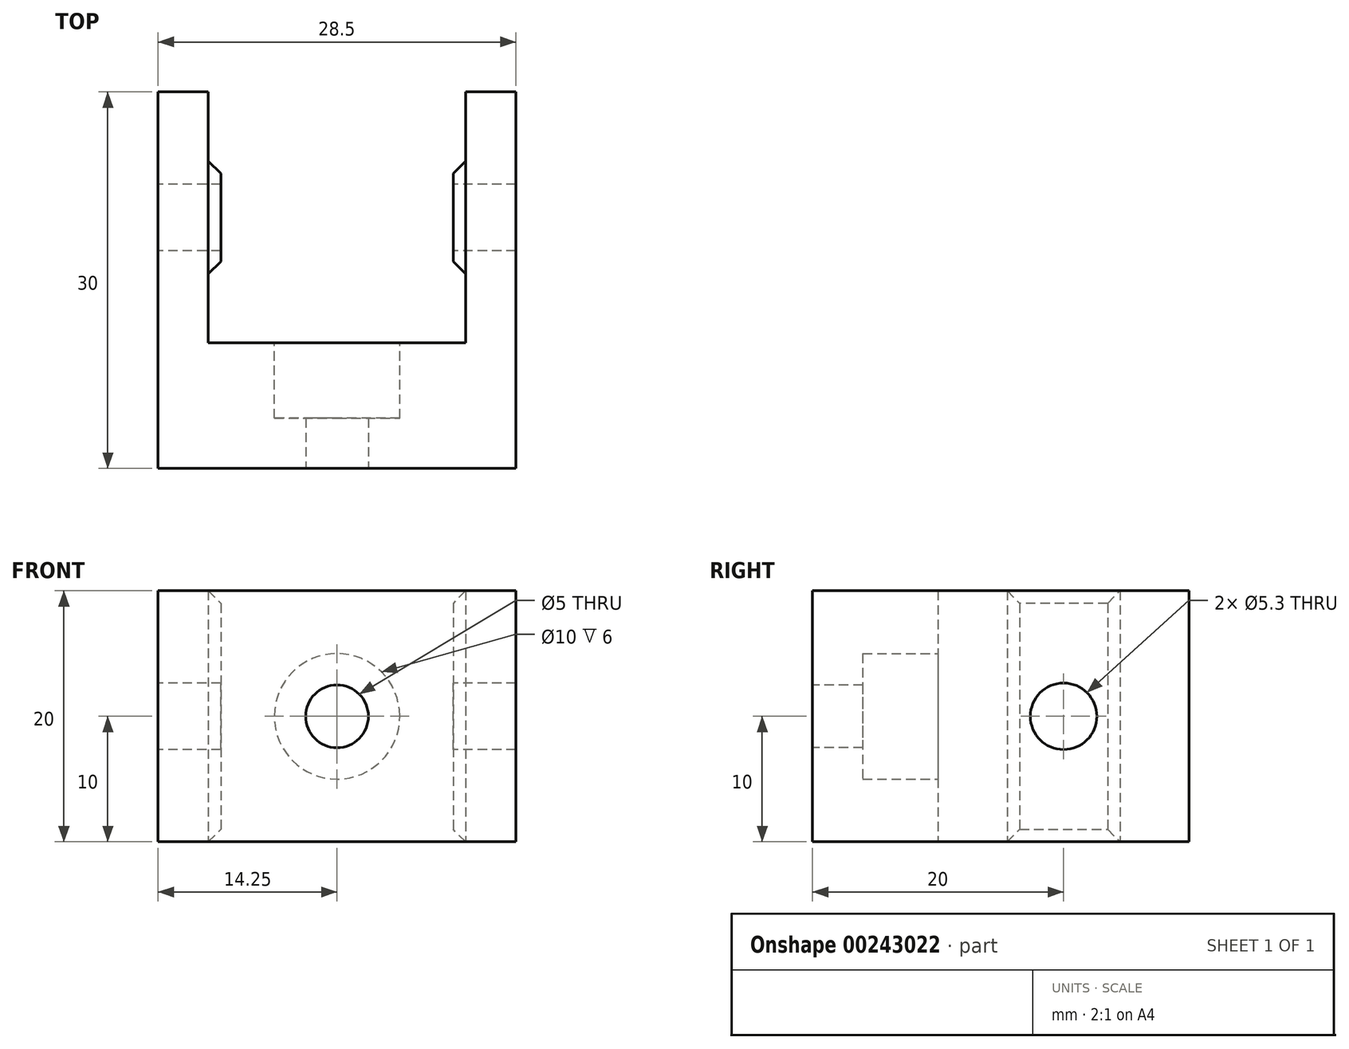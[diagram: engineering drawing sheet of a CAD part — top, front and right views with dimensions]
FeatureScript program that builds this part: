
annotation { "Feature Type Name" : "Feature", "Feature Type Description" : "" }
export const myFeature = defineFeature(function(context is Context, id is Id, definition is map)
    precondition{}
    {
        {
            var Q0;
            Q0=qCreatedBy(makeId("Top.planeOp"),FACE);
            var sketch = newSketch(context, id + "F0", { "sketchPlane" : qUnion([Q0])});
            skLineSegment(sketch, "E0", {"start": v(0, 0) * mm, "end": v(0, 30) * mm});
            skLineSegment(sketch, "E1", {"start": v(0, 30) * mm, "end": v(4, 30) * mm});
            skLineSegment(sketch, "E2", {"start": v(4, 30) * mm, "end": v(4, 10) * mm});
            skLineSegment(sketch, "E3", {"start": v(4, 10) * mm, "end": v(24.5, 10) * mm});
            skLineSegment(sketch, "E4", {"start": v(24.5, 10) * mm, "end": v(24.5, 30) * mm});
            skLineSegment(sketch, "E5", {"start": v(24.5, 30) * mm, "end": v(28.5, 30) * mm});
            skLineSegment(sketch, "E6", {"start": v(28.5, 30) * mm, "end": v(28.5, 0) * mm});
            skLineSegment(sketch, "E7", {"start": v(28.5, 0) * mm, "end": v(0, 0) * mm});
            skSolve(sketch);
        }
        {
            var Q0;
            Q0 = qSketchRegion(id + "F0", true);
            extrude(context, id + "F1", {"entities" : qUnion([Q0]), "depth" : 20 * mm});
        }
        {
            var Q0;
            Q0=qCreatedBy(makeId("Front.planeOp"),FACE);
            var sketch = newSketch(context, id + "F2", { "sketchPlane" : qUnion([Q0])});
            skLineSegment(sketch, "E8.0.0", {"start": v(0, 0) * mm, "end": v(28.5, 0) * mm, "construction": true});
            skLineSegment(sketch, "E8.0.1", {"start": v(28.5, 0) * mm, "end": v(28.5, 20) * mm, "construction": true});
            skLineSegment(sketch, "E8.0.2", {"start": v(28.5, 20) * mm, "end": v(0, 20) * mm, "construction": true});
            skLineSegment(sketch, "E8.0.3", {"start": v(0, 20) * mm, "end": v(0, 0) * mm, "construction": true});
            skCircle(sketch, "E9", {"center": v(14.25, 10) * mm, "radius": 2.5 * mm});
            skPoint(sketch, "E9.centerSnap0", {"position": v(0, 10) * mm});
            skPoint(sketch, "E9.centerSnap1", {"position": v(14.25, 20) * mm});
            skSolve(sketch);
        }
        {
            var Q0;
            Q0 = qSketchRegion(id + "F2", true);
            extrude(context, id + "F3", {"entities" : qUnion([Q0]), "operationType" : NewBodyOperationType.REMOVE, "endBound" : BoundingType.THROUGH_ALL, "oppositeDirection" : true, "depth" : 25 * mm});
        }
        {
            var Q0;
            Q0=makeQuery(id+"F1.opExtrude","SWEPT_FACE",FACE,{"disambiguationData":[OSD([sQuery(id+"F0.wireOp",EDGE,"E3")])]});
            var sketch = newSketch(context, id + "F4", { "sketchPlane" : qUnion([Q0])});
            skCircle(sketch, "E10", {"center": v(-14.25, 10) * mm, "radius": 5 * mm});
            skSolve(sketch);
        }
        {
            var Q0;
            Q0 = qSketchRegion(id + "F4", true);
            extrude(context, id + "F5", {"entities" : qUnion([Q0]), "operationType" : NewBodyOperationType.REMOVE, "oppositeDirection" : true, "depth" : 6 * mm});
        }
        {
            var Q0;
            Q0=qCreatedBy(makeId("Top.planeOp"),FACE);
            var sketch = newSketch(context, id + "F6", { "sketchPlane" : qUnion([Q0])});
            skLineSegment(sketch, "E11.0.0", {"start": v(0, 0) * mm, "end": v(28.5, 0) * mm, "construction": true});
            skLineSegment(sketch, "E11.0.1", {"start": v(28.5, 0) * mm, "end": v(28.5, 30) * mm, "construction": true});
            skLineSegment(sketch, "E11.0.2", {"start": v(28.5, 30) * mm, "end": v(24.5, 30) * mm, "construction": true});
            skLineSegment(sketch, "E11.0.3", {"start": v(24.5, 30) * mm, "end": v(24.5, 10) * mm, "construction": true});
            skLineSegment(sketch, "E11.0.4", {"start": v(24.5, 10) * mm, "end": v(4, 10) * mm, "construction": true});
            skLineSegment(sketch, "E11.0.5", {"start": v(4, 10) * mm, "end": v(4, 30) * mm, "construction": true});
            skLineSegment(sketch, "E11.0.6", {"start": v(4, 30) * mm, "end": v(0, 30) * mm, "construction": true});
            skLineSegment(sketch, "E11.0.7", {"start": v(0, 30) * mm, "end": v(0, 0) * mm, "construction": true});
            skLineSegment(sketch, "E12", {"start": v(4, 15.5) * mm, "end": v(4, 24.5) * mm});
            skLineSegment(sketch, "E13", {"start": v(4, 24.5) * mm, "end": v(5, 23.5) * mm});
            skLineSegment(sketch, "E14", {"start": v(5, 23.5) * mm, "end": v(5, 16.5) * mm});
            skLineSegment(sketch, "E15", {"start": v(4, 15.5) * mm, "end": v(5, 16.5) * mm});
            skLineSegment(sketch, "E16", {"start": v(14.25, 0) * mm, "end": v(14.25, 31.4) * mm, "construction": true});
            skLineSegment(sketch, "E17.MirrorCS", {"start": v(24.5, 15.5) * mm, "end": v(24.5, 24.5) * mm});
            skLineSegment(sketch, "E18.MirrorCS", {"start": v(24.5, 15.5) * mm, "end": v(23.5, 16.5) * mm});
            skLineSegment(sketch, "E19.MirrorCS", {"start": v(23.5, 23.5) * mm, "end": v(23.5, 16.5) * mm});
            skLineSegment(sketch, "E20.MirrorCS", {"start": v(24.5, 24.5) * mm, "end": v(23.5, 23.5) * mm});
            skSolve(sketch);
        }
        {
            var Q0;
            Q0 = qSketchRegion(id + "F6", true);
            var Q1;
            Q1=makeQuery(id+"F1.opExtrude","CAP_FACE",FACE,{"disambiguationData":[OSD([sQuery(id+"F0.wireOp",EDGE,"E0"),sQuery(id+"F0.wireOp",EDGE,"E1"),sQuery(id+"F0.wireOp",EDGE,"E2"),sQuery(id+"F0.wireOp",EDGE,"E3"),sQuery(id+"F0.wireOp",EDGE,"E4"),sQuery(id+"F0.wireOp",EDGE,"E5"),sQuery(id+"F0.wireOp",EDGE,"E6"),sQuery(id+"F0.wireOp",EDGE,"E7")])],"isStart":false});
            extrude(context, id + "F7", {"entities" : qUnion([Q0]), "operationType" : NewBodyOperationType.ADD, "endBound" : BoundingType.UP_TO_SURFACE, "endBoundEntityFace" : qUnion([Q1]), "depth" : 25 * mm});
        }
        {
            var Q0;
            Q0=makeQuery(id+"F7.opExtrude","CAP_EDGE",EDGE,{"disambiguationData":[OSD([sQuery(id+"F6.wireOp",EDGE,"E14")])],"isStart":false});
            var Q1;
            Q1=makeQuery(id+"F7.opExtrude","CAP_EDGE",EDGE,{"disambiguationData":[OSD([sQuery(id+"F6.wireOp",EDGE,"E14")])],"isStart":true});
            var Q2;
            Q2=makeQuery(id+"F7.opExtrude","CAP_EDGE",EDGE,{"disambiguationData":[OSD([sQuery(id+"F6.wireOp",EDGE,"E19.MirrorCS")])],"isStart":false});
            var Q3;
            Q3=makeQuery(id+"F7.opExtrude","CAP_EDGE",EDGE,{"disambiguationData":[OSD([sQuery(id+"F6.wireOp",EDGE,"E19.MirrorCS")])],"isStart":true});
            chamfer(context, id + "F8", {"entities" : qUnion([Q0, Q1, Q2, Q3]), "width" : 1 * mm, "tangentPropagation" : true});
        }
        {
            var Q0;
            Q0=qCreatedBy(makeId("Right.planeOp"),FACE);
            var sketch = newSketch(context, id + "F9", { "sketchPlane" : qUnion([Q0])});
            skLineSegment(sketch, "E21.0.0", {"start": v(16.5, 19) * mm, "end": v(16.5, 1) * mm, "construction": true});
            skLineSegment(sketch, "E21.0.1", {"start": v(16.5, 1) * mm, "end": v(23.5, 1) * mm, "construction": true});
            skLineSegment(sketch, "E21.0.2", {"start": v(23.5, 1) * mm, "end": v(23.5, 19) * mm, "construction": true});
            skLineSegment(sketch, "E21.0.3", {"start": v(23.5, 19) * mm, "end": v(16.5, 19) * mm, "construction": true});
            skCircle(sketch, "E22", {"center": v(20, 10) * mm, "radius": 2.65 * mm});
            skPoint(sketch, "E22.centerSnap0", {"position": v(16.5, 10) * mm});
            skPoint(sketch, "E22.centerSnap1", {"position": v(20, 19) * mm});
            skSolve(sketch);
        }
        {
            var Q0;
            Q0 = qSketchRegion(id + "F9", true);
            extrude(context, id + "F10", {"entities" : qUnion([Q0]), "operationType" : NewBodyOperationType.REMOVE, "endBound" : BoundingType.THROUGH_ALL, "depth" : 25 * mm});
        }
    });
